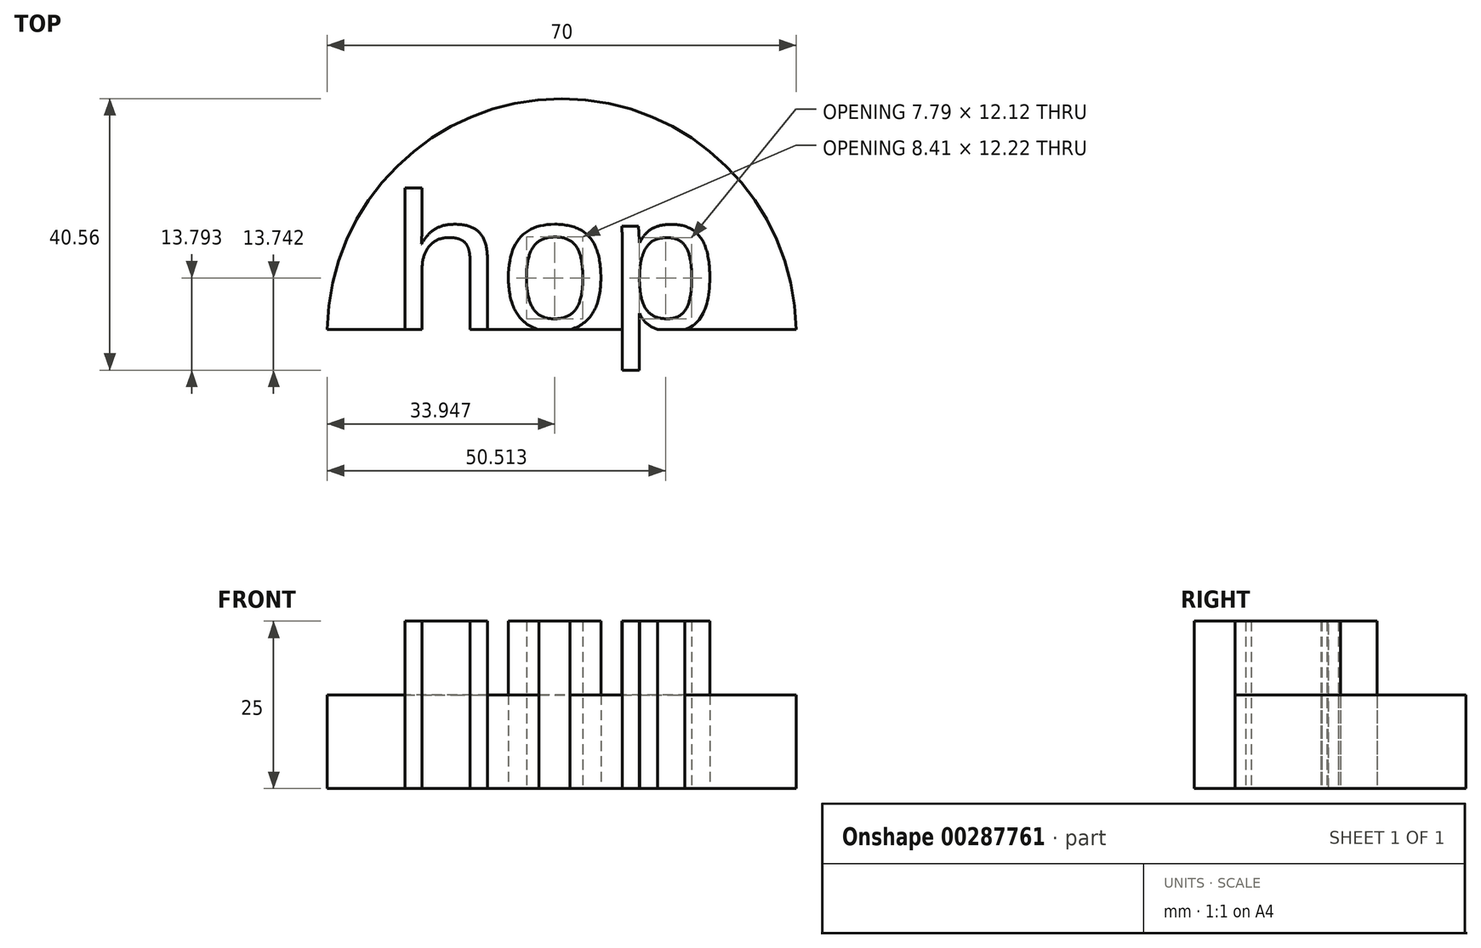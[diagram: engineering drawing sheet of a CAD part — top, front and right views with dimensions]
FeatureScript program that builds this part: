
annotation { "Feature Type Name" : "Feature", "Feature Type Description" : "" }
export const myFeature = defineFeature(function(context is Context, id is Id, definition is map)
    precondition{}
    {
        {
            var Q0;
            Q0=qCreatedBy(makeId("Top.planeOp"),FACE);
            var sketch = newSketch(context, id + "F0", { "sketchPlane" : qUnion([Q0])});
            skLineSegment(sketch, "E0", {"start": v(-24.35, 0) * mm, "end": v(45.65, 0) * mm});
            skArc(sketch, "E1", {"start": v(45.65, 0) * mm, "mid": v(10.65, 34.49) * mm, "end": v(-24.35, 0) * mm});
            skText(sketch, "E2", { "text": "hop", "fontName": "Arimo-Regular.ttf"});
            const initialGuessF0  = {"E2": [-0.01479, 0, 1, 0, 0.02105]};
            skSetInitialGuess(sketch, initialGuessF0);
            skSolve(sketch);
        }
        {
            var Q0;
            Q0=makeQuery(id+"F0.imprint","IMPRINT",FACE,{"disambiguationData":[TD([[makeQuery(id+"F0.imprint","IMPRINT",EDGE,{"derivedFrom":sQuery(id+"F0.wireOp",EDGE,"E2.sketch_text.stroke-0")}),-1.0]])]});
            var Q1;
            {var subQ6=sQuery(id+"F0.wireOp",EDGE,"E2.sketch_text.stroke-20");Q1=makeQuery(id+"F0.imprint","IMPRINT",FACE,{"disambiguationData":[TD([[makeQuery(id+"F0.imprint","IMPRINT",EDGE,{"derivedFrom":subQ6}),-1.0]])]});}
            var Q2;
            {var subQ7=sQuery(id+"F0.wireOp",EDGE,"E2.sketch_text.stroke-37");Q2=makeQuery(id+"F0.imprint","IMPRINT",FACE,{"disambiguationData":[TD([[makeQuery(id+"F0.imprint","IMPRINT",EDGE,{"derivedFrom":subQ7}),-1.0]])]});}
            var Q3;
            {var subQ0=sQuery(id+"F0.wireOp",EDGE,"E2.sketch_text.stroke-39");Q3=makeQuery(id+"F0.imprint","IMPRINT",FACE,{"disambiguationData":[TD([[makeQuery(id+"F0.imprint","IMPRINT",EDGE,{"derivedFrom":subQ0}),-1.0]])]});}
            extrude(context, id + "F1", {"entities" : qUnion([Q0, Q1, Q2, Q3]), "depth" : 25 * mm});
        }
        {
            var Q0;
            {var subQ5=sQuery(id+"F0.wireOp",EDGE,"E1");Q0=makeQuery(id+"F0.imprint","IMPRINT",FACE,{"disambiguationData":[TD([[makeQuery(id+"F0.imprint","IMPRINT",EDGE,{"derivedFrom":subQ5}),1.0]])]});}
            extrude(context, id + "F2", {"entities" : qUnion([Q0]), "depth" : 14 * mm});
        }
    });
